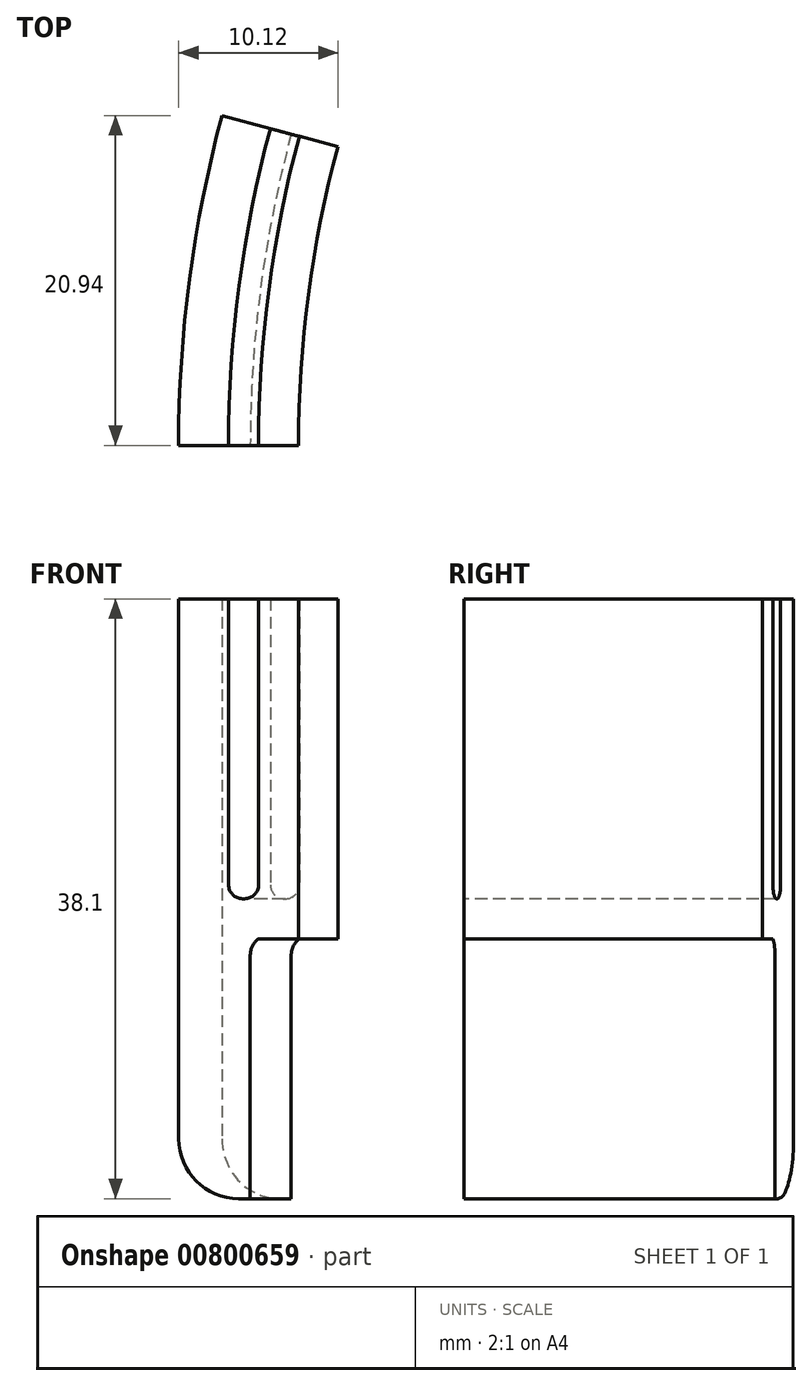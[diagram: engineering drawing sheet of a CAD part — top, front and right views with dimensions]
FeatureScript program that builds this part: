
annotation { "Feature Type Name" : "Feature", "Feature Type Description" : "" }
export const myFeature = defineFeature(function(context is Context, id is Id, definition is map)
    precondition{}
    {
        {
            var Q0;
            Q0=qCreatedBy(makeId("Top.planeOp"),FACE);
            var sketch = newSketch(context, id + "F0", { "sketchPlane" : qUnion([Q0])});
            skCircle(sketch, "E0", {"center": v(0, 0) * mm, "radius": 75.82 * mm});
            skCircle(sketch, "E1", {"center": v(0, 0) * mm, "radius": 77.72 * mm});
            skCircle(sketch, "E2", {"center": v(0, 0) * mm, "radius": 73.28 * mm});
            skCircle(sketch, "E3", {"center": v(0, 0) * mm, "radius": 80.9 * mm});
            skSolve(sketch);
        }
        {
            var Q0;
            Q0=makeQuery(id+"F0.imprint","IMPRINT",FACE,{"disambiguationData":[TD([[makeQuery(id+"F0.imprint","IMPRINT",EDGE,{"derivedFrom":sQuery(id+"F0.wireOp",EDGE,"E1")}),-1.0]])]});
            var Q1;
            Q1=makeQuery(id+"F0.imprint","IMPRINT",FACE,{"disambiguationData":[TD([[makeQuery(id+"F0.imprint","IMPRINT",EDGE,{"derivedFrom":sQuery(id+"F0.wireOp",EDGE,"E0")}),1.0]])]});
            extrude(context, id + "F1", {"entities" : qUnion([Q0, Q1]), "depth" : 38.1 * mm, "offsetDistance" : 25.4 * mm});
        }
        {
            var Q0;
            Q0=makeQuery(id+"F0.imprint","IMPRINT",FACE,{"disambiguationData":[TD([[makeQuery(id+"F0.imprint","IMPRINT",EDGE,{"derivedFrom":sQuery(id+"F0.wireOp",EDGE,"E0")}),-1.0]])]});
            extrude(context, id + "F2", {"entities" : qUnion([Q0]), "depth" : 19.05 * mm, "offsetDistance" : 25.4 * mm});
        }
        {
            var Q0;
            Q0=qCreatedBy(makeId("Front.planeOp"),FACE);
            var sketch = newSketch(context, id + "F3", { "sketchPlane" : qUnion([Q0])});
            skLineSegment(sketch, "E4.bottom", {"start": v(-65.2, 0) * mm, "end": v(-87.9, 0) * mm});
            skLineSegment(sketch, "E4.top", {"start": v(-65.2, 49.68) * mm, "end": v(-87.9, 49.68) * mm});
            skLineSegment(sketch, "E4.left", {"start": v(-65.2, 0) * mm, "end": v(-65.2, 49.68) * mm});
            skLineSegment(sketch, "E4.right", {"start": v(-87.9, 0) * mm, "end": v(-87.9, 49.68) * mm});
            skLineSegment(sketch, "E5", {"start": v(0, 42.78) * mm, "end": v(0, 34.78) * mm, "construction": true});
            skSolve(sketch);
        }
        {
            var Q0;
            Q0=makeQuery(id+"F3.imprint","IMPRINT",FACE,{"disambiguationData":[TD([[makeQuery(id+"F3.imprint","IMPRINT",EDGE,{"derivedFrom":sQuery(id+"F3.wireOp",EDGE,"E4.bottom")}),-1.0]])]});
            var Q1;
            Q1=sQuery(id+"F3.wireOp",EDGE,"E5");
            revolve(context, id + "F4", {"operationType" : NewBodyOperationType.INTERSECT, "surfaceOperationType" : NewSurfaceOperationType.NEW, "entities" : qUnion([Q0]), "axis" : qUnion([Q1]), "revolveType" : RevolveType.ONE_DIRECTION, "angle" : 15 * degree});
        }
        {
            var Q0;
            Q0=qCreatedBy(makeId("Top.planeOp"),FACE);
            var sketch = newSketch(context, id + "F5", { "sketchPlane" : qUnion([Q0])});
            skCircle(sketch, "E6", {"center": v(0, 0) * mm, "radius": 76.35 * mm});
            skSolve(sketch);
        }
        {
            var Q0;
            Q0=makeQuery(id+"F5.imprint","IMPRINT",FACE,{"disambiguationData":[TD([[makeQuery(id+"F5.imprint","IMPRINT",EDGE,{"derivedFrom":sQuery(id+"F5.wireOp",EDGE,"E6")}),1.0]])]});
            extrude(context, id + "F6", {"entities" : qUnion([Q0]), "operationType" : NewBodyOperationType.REMOVE, "depth" : 16.5 * mm, "offsetDistance" : 25.4 * mm});
        }
        {
            var Q0;
            Q0=makeQuery(id+"F6.boolean.opBoolean","COPY",EDGE,{"derivedFrom":makeQuery(id+"F6.opExtrude","CAP_EDGE",EDGE,{"disambiguationData":[OSD([sQuery(id+"F5.wireOp",EDGE,"E6")])],"isStart":false})});
            fillet(context, id + "F7", {"entities" : qUnion([Q0]), "radius" : 1.27 * mm, "tangentPropagation" : true, "allowEdgeOverflow" : false});
        }
        {
            var Q0;
            Q0=qCreatedBy(makeId("Front.planeOp"),FACE);
            var sketch = newSketch(context, id + "F8", { "sketchPlane" : qUnion([Q0])});
            skLineSegment(sketch, "E7.0.0", {"start": v(-77.72, 38.1) * mm, "end": v(-80.9, 38.1) * mm});
            skLineSegment(sketch, "E7.0.1", {"start": v(-80.9, 38.1) * mm, "end": v(-80.9, 0) * mm});
            skLineSegment(sketch, "E7.0.2", {"start": v(-80.9, 0) * mm, "end": v(-77.72, 0) * mm});
            skLineSegment(sketch, "E7.0.3", {"start": v(-77.72, 0) * mm, "end": v(-77.72, 38.1) * mm});
            skLineSegment(sketch, "E8.0.0", {"start": v(-77.72, 0) * mm, "end": v(-76.35, 0) * mm});
            skLineSegment(sketch, "E8.0.1", {"start": v(-76.35, 0) * mm, "end": v(-76.35, 15.48) * mm});
            skArc(sketch, "E8.0.2", {"start": v(-76.35, 15.48) * mm, "mid": v(-76.2, 16.06) * mm, "end": v(-75.82, 16.51) * mm});
            skLineSegment(sketch, "E8.0.3", {"start": v(-75.82, 16.51) * mm, "end": v(-75.82, 19.05) * mm});
            skLineSegment(sketch, "E8.0.4", {"start": v(-75.82, 19.05) * mm, "end": v(-77.72, 19.05) * mm});
            skLineSegment(sketch, "E8.0.5", {"start": v(-77.72, 19.05) * mm, "end": v(-77.72, 0) * mm});
            skLineSegment(sketch, "E9.0.0", {"start": v(-75.82, 16.51) * mm, "end": v(-73.28, 16.51) * mm});
            skLineSegment(sketch, "E9.0.1", {"start": v(-73.28, 16.51) * mm, "end": v(-73.28, 38.1) * mm});
            skLineSegment(sketch, "E9.0.2", {"start": v(-73.28, 38.1) * mm, "end": v(-75.82, 38.1) * mm});
            skLineSegment(sketch, "E9.0.3", {"start": v(-75.82, 38.1) * mm, "end": v(-75.82, 16.51) * mm});
            skLineSegment(sketch, "E10.bottom", {"start": v(-77.72, 19.05) * mm, "end": v(-79.6, 19.05) * mm});
            skLineSegment(sketch, "E10.top", {"start": v(-77.72, 24.27) * mm, "end": v(-79.6, 24.27) * mm});
            skLineSegment(sketch, "E10.left", {"start": v(-77.72, 19.94) * mm, "end": v(-77.72, 24.27) * mm});
            skLineSegment(sketch, "E10.right", {"start": v(-79.6, 19.05) * mm, "end": v(-79.6, 24.27) * mm});
            skLineSegment(sketch, "E11.bottom", {"start": v(-75.82, 19.05) * mm, "end": v(-73.77, 19.05) * mm});
            skLineSegment(sketch, "E11.top", {"start": v(-75.82, 24.58) * mm, "end": v(-73.77, 24.58) * mm});
            skLineSegment(sketch, "E11.left", {"start": v(-75.82, 19.94) * mm, "end": v(-75.82, 24.58) * mm});
            skLineSegment(sketch, "E11.right", {"start": v(-73.77, 19.05) * mm, "end": v(-73.77, 24.58) * mm});
            skLineSegment(sketch, "E12.bottom", {"start": v(-76.83, 19.05) * mm, "end": v(-76.7, 19.05) * mm});
            skLineSegment(sketch, "E12.top", {"start": v(-79.6, 16.51) * mm, "end": v(-73.77, 16.51) * mm});
            skLineSegment(sketch, "E12.left", {"start": v(-79.6, 19.05) * mm, "end": v(-79.6, 16.51) * mm});
            skLineSegment(sketch, "E12.right", {"start": v(-73.77, 19.05) * mm, "end": v(-73.77, 16.51) * mm});
            skArc(sketch, "E13.filletArc", {"start": v(-77.72, 19.94) * mm, "mid": v(-77.46, 19.31) * mm, "end": v(-76.83, 19.05) * mm});
            skPoint(sketch, "E14.newPointA", {"position": v(-73.77, 19.05) * mm});
            skArc(sketch, "E14.filletArc", {"start": v(-76.7, 19.05) * mm, "mid": v(-76.08, 19.31) * mm, "end": v(-75.82, 19.94) * mm});
            skSolve(sketch);
        }
        {
            var Q0;
            {var subQ3=sQuery(id+"F8.wireOp",EDGE,"E14.filletArc");Q0=makeQuery(id+"F8.imprint","IMPRINT",FACE,{"disambiguationData":[TD([[makeQuery(id+"F8.imprint","IMPRINT",EDGE,{"derivedFrom":subQ3}),-1.0]])]});}
            var Q1;
            {var subQ3=sQuery(id+"F8.wireOp",EDGE,"E13.filletArc");Q1=makeQuery(id+"F8.imprint","IMPRINT",FACE,{"disambiguationData":[TD([[makeQuery(id+"F8.imprint","IMPRINT",EDGE,{"derivedFrom":subQ3}),-1.0]])]});}
            var Q2;
            Q2=sQuery(id+"F3.wireOp",EDGE,"E5");
            revolve(context, id + "F9", {"operationType" : NewBodyOperationType.ADD, "surfaceOperationType" : NewSurfaceOperationType.NEW, "entities" : qUnion([Q0, Q1]), "axis" : qUnion([Q2]), "revolveType" : RevolveType.ONE_DIRECTION, "angle" : 15 * degree});
        }
        {
            var Q0;
            Q0=makeQuery(id+"F1.opExtrude","CAP_EDGE",EDGE,{"disambiguationData":[OSD([sQuery(id+"F0.wireOp",EDGE,"E3")])],"isStart":true});
            fillet(context, id + "F10", {"entities" : qUnion([Q0]), "radius" : 3.8 * mm, "tangentPropagation" : true, "allowEdgeOverflow" : false});
        }
    });
